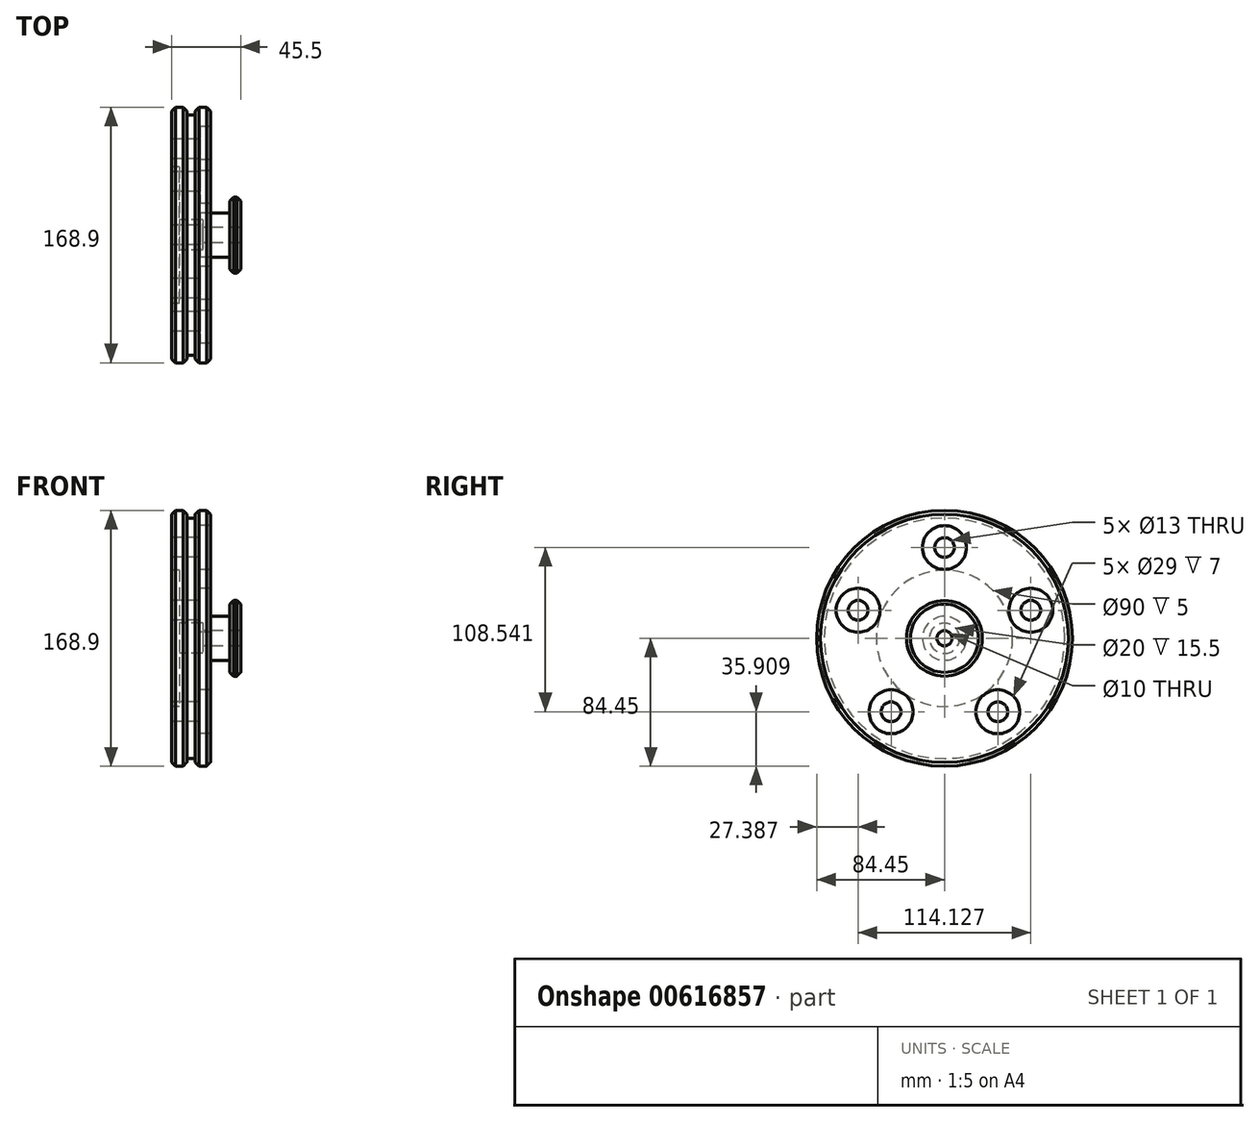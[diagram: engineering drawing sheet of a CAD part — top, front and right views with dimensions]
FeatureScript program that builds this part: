
annotation { "Feature Type Name" : "Feature", "Feature Type Description" : "" }
export const myFeature = defineFeature(function(context is Context, id is Id, definition is map)
    precondition{}
    {
        {
            var Q0;
            Q0=qCreatedBy(makeId("Front.planeOp"),FACE);
            var sketch = newSketch(context, id + "F0", { "sketchPlane" : qUnion([Q0])});
            skLineSegment(sketch, "E0", {"start": v(0, 45) * mm, "end": v(0, 84.45) * mm});
            skLineSegment(sketch, "E1", {"start": v(0, 84.45) * mm, "end": v(10, 84.45) * mm});
            skLineSegment(sketch, "E2", {"start": v(25.5, 84.45) * mm, "end": v(25.5, 14.5) * mm});
            skLineSegment(sketch, "E3", {"start": v(25.5, 14.5) * mm, "end": v(38.3, 14.5) * mm});
            skLineSegment(sketch, "E4", {"start": v(38.3, 14.5) * mm, "end": v(38.3, 25) * mm});
            skLineSegment(sketch, "E5", {"start": v(38.3, 25) * mm, "end": v(45.5, 25) * mm});
            skLineSegment(sketch, "E6", {"start": v(45.5, 25) * mm, "end": v(45.5, 5) * mm});
            skLineSegment(sketch, "E7", {"start": v(45.5, 5) * mm, "end": v(20.5, 5) * mm});
            skLineSegment(sketch, "E8", {"start": v(20.5, 5) * mm, "end": v(20.5, 10) * mm});
            skLineSegment(sketch, "E9", {"start": v(20.5, 10) * mm, "end": v(5, 10) * mm});
            skLineSegment(sketch, "E10", {"start": v(5, 10) * mm, "end": v(5, 45) * mm});
            skLineSegment(sketch, "E11", {"start": v(5, 45) * mm, "end": v(0, 45) * mm});
            skLineSegment(sketch, "E12", {"start": v(10, 84.45) * mm, "end": v(10, 79.45) * mm});
            skLineSegment(sketch, "E13", {"start": v(10, 79.45) * mm, "end": v(15.5, 79.45) * mm});
            skLineSegment(sketch, "E14", {"start": v(15.5, 79.45) * mm, "end": v(15.5, 84.45) * mm});
            skLineSegment(sketch, "E15.trimOffspring", {"start": v(15.5, 84.45) * mm, "end": v(25.5, 84.45) * mm});
            skLineSegment(sketch, "E16", {"start": v(0, 0) * mm, "end": v(72.05, 0) * mm, "construction": true});
            skSolve(sketch);
        }
        {
            var Q0;
            Q0=makeQuery(id+"F0.imprint","IMPRINT",FACE,{"disambiguationData":[TD([[makeQuery(id+"F0.imprint","IMPRINT",EDGE,{"derivedFrom":sQuery(id+"F0.wireOp",EDGE,"E0")}),-1.0]])]});
            var Q1;
            Q1=sQuery(id+"F0.wireOp",EDGE,"E16");
            revolve(context, id + "F1", {"surfaceOperationType" : NewSurfaceOperationType.NEW, "entities" : qUnion([Q0]), "axis" : qUnion([Q1]), "revolveType" : RevolveType.FULL});
        }
        {
            var Q0;
            Q0=makeQuery(id+"F1.opRevolve","SWEPT_EDGE",EDGE,{"disambiguationData":[OSD([sQuery(id+"F0.wireOp",EDGE,"E2"),sQuery(id+"F0.wireOp",EDGE,"E15.trimOffspring")])]});
            var Q1;
            Q1=makeQuery(id+"F1.opRevolve","SWEPT_EDGE",EDGE,{"disambiguationData":[OSD([sQuery(id+"F0.wireOp",EDGE,"E14"),sQuery(id+"F0.wireOp",EDGE,"E15.trimOffspring")])]});
            var Q2;
            Q2=makeQuery(id+"F1.opRevolve","SWEPT_EDGE",EDGE,{"disambiguationData":[OSD([sQuery(id+"F0.wireOp",EDGE,"E1"),sQuery(id+"F0.wireOp",EDGE,"E12")])]});
            var Q3;
            Q3=makeQuery(id+"F1.opRevolve","SWEPT_EDGE",EDGE,{"disambiguationData":[OSD([sQuery(id+"F0.wireOp",EDGE,"E0"),sQuery(id+"F0.wireOp",EDGE,"E1")])]});
            chamfer(context, id + "F2", {"entities" : qUnion([Q0, Q1, Q2, Q3]), "width" : 2.5 * mm, "tangentPropagation" : true});
        }
        {
            var Q0;
            Q0=qCreatedBy(makeId("Right.planeOp"),FACE);
            var sketch = newSketch(context, id + "F3", { "sketchPlane" : qUnion([Q0])});
            skCircle(sketch, "E17", {"center": v(0, 0) * mm, "radius": 60 * mm, "construction": true});
            skCircle(sketch, "E18", {"center": v(0, 60) * mm, "radius": 14.5 * mm});
            skCircle(sketch, "E19", {"center": v(0, 60) * mm, "radius": 6.5 * mm});
            skCircle(sketch, "E20.1.0", {"center": v(-57.06, 18.54) * mm, "radius": 14.5 * mm});
            skCircle(sketch, "E20.1.1", {"center": v(-57.06, 18.54) * mm, "radius": 6.5 * mm});
            skCircle(sketch, "E20.2.0", {"center": v(-35.27, -48.54) * mm, "radius": 14.5 * mm});
            skCircle(sketch, "E20.2.1", {"center": v(-35.27, -48.54) * mm, "radius": 6.5 * mm});
            skCircle(sketch, "E20.3.0", {"center": v(35.27, -48.54) * mm, "radius": 14.5 * mm});
            skCircle(sketch, "E20.3.1", {"center": v(35.27, -48.54) * mm, "radius": 6.5 * mm});
            skCircle(sketch, "E20.4.0", {"center": v(57.06, 18.54) * mm, "radius": 14.5 * mm});
            skCircle(sketch, "E20.4.1", {"center": v(57.06, 18.54) * mm, "radius": 6.5 * mm});
            skSolve(sketch);
        }
        {
            var Q0;
            Q0=makeQuery(id+"F3.imprint","IMPRINT",FACE,{"disambiguationData":[TD([[makeQuery(id+"F3.imprint","IMPRINT",EDGE,{"derivedFrom":sQuery(id+"F3.wireOp",EDGE,"E20.4.1")}),1.0]])]});
            var Q1;
            Q1=makeQuery(id+"F3.imprint","IMPRINT",FACE,{"disambiguationData":[TD([[makeQuery(id+"F3.imprint","IMPRINT",EDGE,{"derivedFrom":sQuery(id+"F3.wireOp",EDGE,"E20.3.1")}),1.0]])]});
            var Q2;
            Q2=makeQuery(id+"F3.imprint","IMPRINT",FACE,{"disambiguationData":[TD([[makeQuery(id+"F3.imprint","IMPRINT",EDGE,{"derivedFrom":sQuery(id+"F3.wireOp",EDGE,"E20.2.1")}),1.0]])]});
            var Q3;
            Q3=makeQuery(id+"F3.imprint","IMPRINT",FACE,{"disambiguationData":[TD([[makeQuery(id+"F3.imprint","IMPRINT",EDGE,{"derivedFrom":sQuery(id+"F3.wireOp",EDGE,"E20.1.1")}),1.0]])]});
            var Q4;
            Q4=makeQuery(id+"F3.imprint","IMPRINT",FACE,{"disambiguationData":[TD([[makeQuery(id+"F3.imprint","IMPRINT",EDGE,{"derivedFrom":sQuery(id+"F3.wireOp",EDGE,"E19")}),1.0]])]});
            extrude(context, id + "F4", {"entities" : qUnion([Q0, Q1, Q2, Q3, Q4]), "operationType" : NewBodyOperationType.REMOVE, "endBound" : BoundingType.THROUGH_ALL, "depth" : 25 * mm, "offsetDistance" : 25 * mm});
        }
        {
            var Q0;
            Q0=makeQuery(id+"F3.imprint","IMPRINT",FACE,{"disambiguationData":[TD([[makeQuery(id+"F3.imprint","IMPRINT",EDGE,{"derivedFrom":sQuery(id+"F3.wireOp",EDGE,"E18")}),1.0]])]});
            var Q1;
            Q1=makeQuery(id+"F3.imprint","IMPRINT",FACE,{"disambiguationData":[TD([[makeQuery(id+"F3.imprint","IMPRINT",EDGE,{"derivedFrom":sQuery(id+"F3.wireOp",EDGE,"E20.1.0")}),1.0]])]});
            var Q2;
            Q2=makeQuery(id+"F3.imprint","IMPRINT",FACE,{"disambiguationData":[TD([[makeQuery(id+"F3.imprint","IMPRINT",EDGE,{"derivedFrom":sQuery(id+"F3.wireOp",EDGE,"E20.2.0")}),1.0]])]});
            var Q3;
            Q3=makeQuery(id+"F3.imprint","IMPRINT",FACE,{"disambiguationData":[TD([[makeQuery(id+"F3.imprint","IMPRINT",EDGE,{"derivedFrom":sQuery(id+"F3.wireOp",EDGE,"E20.3.0")}),1.0]])]});
            var Q4;
            Q4=makeQuery(id+"F3.imprint","IMPRINT",FACE,{"disambiguationData":[TD([[makeQuery(id+"F3.imprint","IMPRINT",EDGE,{"derivedFrom":sQuery(id+"F3.wireOp",EDGE,"E20.4.0")}),1.0]])]});
            var Q5;
            Q5=makeQuery(id+"F1.opRevolve","SWEPT_FACE",FACE,{"disambiguationData":[OSD([sQuery(id+"F0.wireOp",EDGE,"E2")])]});
            extrude(context, id + "F5", {"entities" : qUnion([Q0, Q1, Q2, Q3, Q4]), "operationType" : NewBodyOperationType.REMOVE, "endBound" : BoundingType.UP_TO_SURFACE, "depth" : 25 * mm, "endBoundEntityFace" : qUnion([Q5]), "offsetDistance" : 7 * mm, "hasSecondDirection" : true, "secondDirectionOppositeDirection" : false, "secondDirectionDepth" : 18.5 * mm});
        }
        {
            var Q0;
            Q0=makeQuery(id+"F1.opRevolve","SWEPT_EDGE",EDGE,{"disambiguationData":[OSD([sQuery(id+"F0.wireOp",EDGE,"E5"),sQuery(id+"F0.wireOp",EDGE,"E6")])]});
            var Q1;
            Q1=makeQuery(id+"F1.opRevolve","SWEPT_EDGE",EDGE,{"disambiguationData":[OSD([sQuery(id+"F0.wireOp",EDGE,"E4"),sQuery(id+"F0.wireOp",EDGE,"E5")])]});
            chamfer(context, id + "F6", {"entities" : qUnion([Q0, Q1]), "width" : 2.5 * mm, "tangentPropagation" : true});
        }
    });
